# Revit family: HPLp60
name_source: partatom
category: 機械設備
units: mm (PartAtom-declared; Revit-internal decimal feet)

## family parameters
OmniClass タイトル = Climate Control (HVAC)
OmniClass 番号 = 23.75.00.00
パーツ タイプ = 標準
ロード時にボイドで切り取り = いいえ
丸型コネクタ寸法 = 直径を使用
作業面ベース = いいえ
共有 = はい
常に垂直 = はい
部屋計算ポイント = いいえ

## types (10) — shared parameters
フランジT = 60  [stored 0.19685 ft]
フランジ厚 = 60  [stored 0.19685 ft]
zero-valued in all types: 既定の高さ

## per-type parameters (varying)
| type | 先行ピース |
| C60x30x10x1.4 | 先行ﾋﾟｰｽ : C60x30x10x1.4 |
| C60x30x10x2.3 | 先行ﾋﾟｰｽ : C60x30x10x2.3 |
| C65x30x10x1.4 | 先行ﾋﾟｰｽ : C65x30x10x1.4 |
| C65x30x10x2.3 | 先行ﾋﾟｰｽ : C65x30x10x2.3 |
| C75x45x15x1.4 | 先行ﾋﾟｰｽ : C75x45x15x1.4 |
| C75x45x15x2.3 | 先行ﾋﾟｰｽ : C75x45x15x2.3 |
| C90x45x15x1.4 | 先行ﾋﾟｰｽ : C90x45x15x1.4 |
| C90x45x15x2.3 | 先行ﾋﾟｰｽ : C90x45x15x2.3 |
| C100x50x20x1.4 | 先行ﾋﾟｰｽ : C100x50x20x1.4 |
| C100x50x20x2.3 | 先行ﾋﾟｰｽ : C100x50x20x2.3 |

note: [stored X ft] marks values corroborated as IEEE doubles in the binary element streams (Revit-internal decimal feet)
